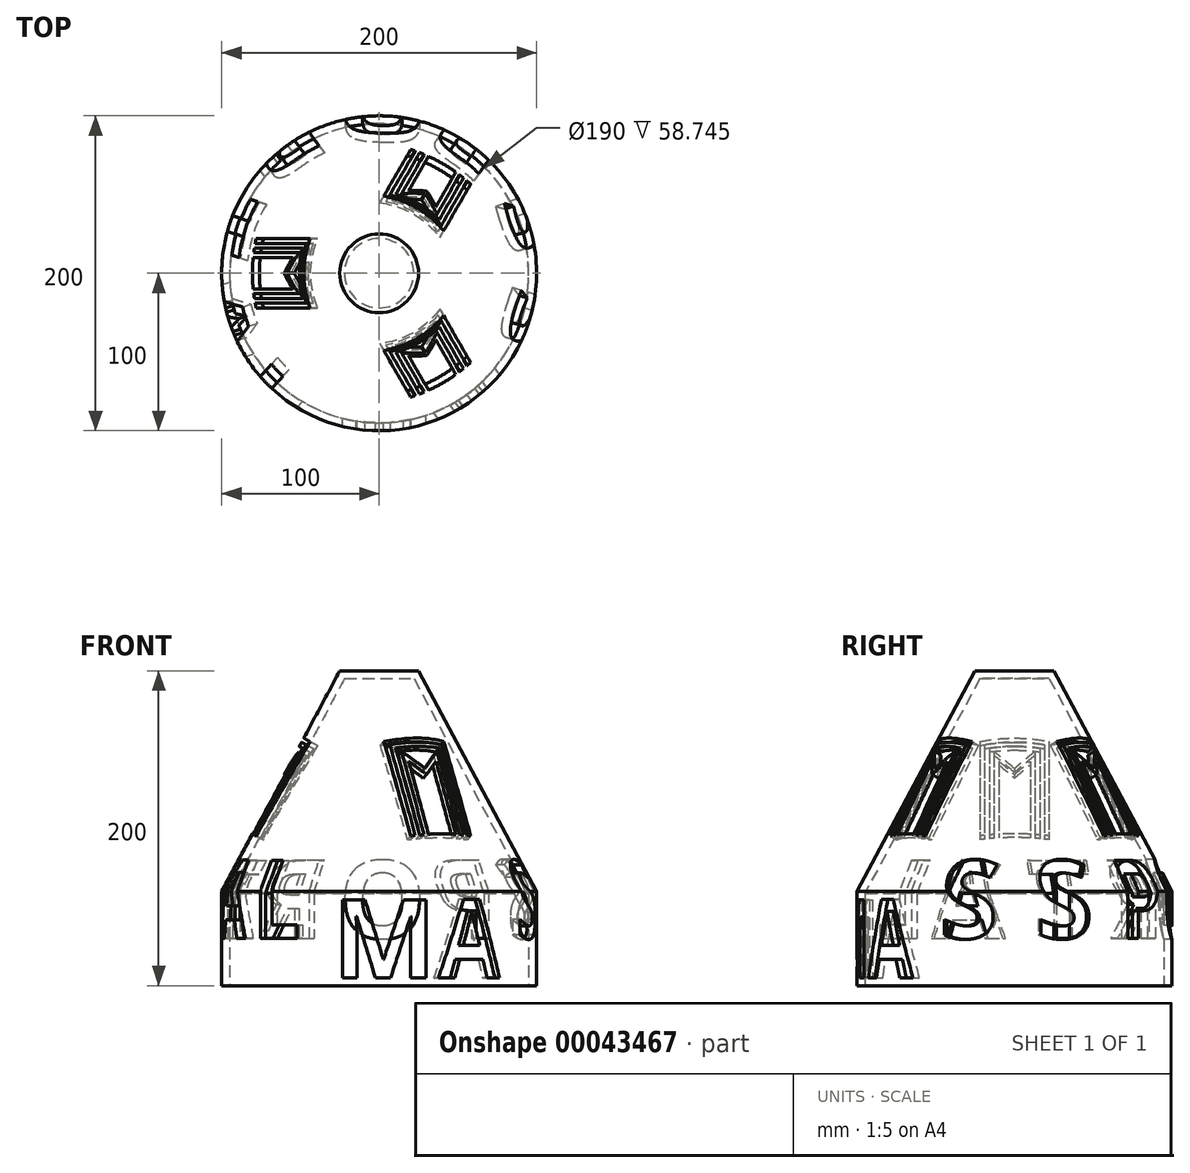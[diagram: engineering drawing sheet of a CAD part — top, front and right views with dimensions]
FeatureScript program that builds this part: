
annotation { "Feature Type Name" : "Feature", "Feature Type Description" : "" }
export const myFeature = defineFeature(function(context is Context, id is Id, definition is map)
    precondition{}
    {
        {
            var Q0;
            Q0=qCreatedBy(makeId("Front.planeOp"),FACE);
            var sketch = newSketch(context, id + "F0", { "sketchPlane" : qUnion([Q0])});
            skLineSegment(sketch, "E0", {"start": v(0, 0) * mm, "end": v(0, 200) * mm, "construction": true});
            skLineSegment(sketch, "E1", {"start": v(0, 200) * mm, "end": v(-25, 200) * mm});
            skLineSegment(sketch, "E2", {"start": v(-25, 200) * mm, "end": v(-100, 60) * mm});
            skLineSegment(sketch, "E3", {"start": v(-100, 60) * mm, "end": v(-100, 0) * mm});
            skLineSegment(sketch, "E4.0", {"start": v(-95, 58.75) * mm, "end": v(-95, 0) * mm});
            skLineSegment(sketch, "E4.1", {"start": v(-22, 195) * mm, "end": v(-95, 58.75) * mm});
            skLineSegment(sketch, "E4.2", {"start": v(0, 195) * mm, "end": v(-22, 195) * mm});
            skLineSegment(sketch, "E5", {"start": v(-100, 0) * mm, "end": v(-95, 0) * mm});
            skLineSegment(sketch, "E6", {"start": v(0, 200) * mm, "end": v(0, 195) * mm});
            skSolve(sketch);
        }
        {
            var Q0;
            Q0=makeQuery(id+"F0.imprint","IMPRINT",FACE,{"disambiguationData":[TD([[makeQuery(id+"F0.imprint","IMPRINT",EDGE,{"derivedFrom":sQuery(id+"F0.wireOp",EDGE,"E1")}),1.0]])]});
            var Q1;
            Q1=sQuery(id+"F0.wireOp",EDGE,"E0");
            revolve(context, id + "F1", {"entities" : qUnion([Q0]), "axis" : qUnion([Q1]), "revolveType" : RevolveType.FULL});
        }
        {
            var Q0;
            Q0=qCreatedBy(makeId("Front.planeOp"),FACE);
            var Q1;
            Q1=sQuery(id+"F0.wireOp",EDGE,"E0");
            cPlane(context, id + "F2", {"entities" : qUnion([Q0, Q1]), "cplaneType" : CPlaneType.LINE_ANGLE, "offset" : 150 * mm, "angle" : 36 * degree, "width" : 150 * mm, "height" : 150 * mm});
        }
        {
            var Q0;
            Q0=qCreatedBy(id+"F2.planeOp",FACE);
            var Q1;
            Q1=sQuery(id+"F0.wireOp",EDGE,"E0");
            cPlane(context, id + "F3", {"entities" : qUnion([Q0, Q1]), "cplaneType" : CPlaneType.LINE_ANGLE, "offset" : 150 * mm, "angle" : 36 * degree, "width" : 150 * mm, "height" : 150 * mm});
        }
        {
            var Q0;
            Q0=qCreatedBy(id+"F3.planeOp",FACE);
            var Q1;
            Q1=sQuery(id+"F0.wireOp",EDGE,"E0");
            cPlane(context, id + "F4", {"entities" : qUnion([Q0, Q1]), "cplaneType" : CPlaneType.LINE_ANGLE, "offset" : 150 * mm, "angle" : 36 * degree, "width" : 150 * mm, "height" : 150 * mm});
        }
        {
            var Q0;
            Q0=qCreatedBy(id+"F4.planeOp",FACE);
            var Q1;
            Q1=sQuery(id+"F0.wireOp",EDGE,"E0");
            cPlane(context, id + "F5", {"entities" : qUnion([Q0, Q1]), "cplaneType" : CPlaneType.LINE_ANGLE, "offset" : 150 * mm, "angle" : 36 * degree, "width" : 150 * mm, "height" : 150 * mm});
        }
        {
            var Q0;
            Q0=qCreatedBy(id+"F5.planeOp",FACE);
            var Q1;
            Q1=sQuery(id+"F0.wireOp",EDGE,"E0");
            cPlane(context, id + "F6", {"entities" : qUnion([Q0, Q1]), "cplaneType" : CPlaneType.LINE_ANGLE, "offset" : 150 * mm, "angle" : 36 * degree, "width" : 150 * mm, "height" : 150 * mm});
        }
        {
            var Q0;
            Q0=qCreatedBy(id+"F6.planeOp",FACE);
            var Q1;
            Q1=sQuery(id+"F0.wireOp",EDGE,"E0");
            cPlane(context, id + "F7", {"entities" : qUnion([Q0, Q1]), "cplaneType" : CPlaneType.LINE_ANGLE, "offset" : 150 * mm, "angle" : 36 * degree, "width" : 150 * mm, "height" : 150 * mm});
        }
        {
            var Q0;
            Q0=sQuery(id+"F0.wireOp",EDGE,"E0");
            var Q1;
            Q1=qCreatedBy(id+"F7.planeOp",FACE);
            cPlane(context, id + "F8", {"entities" : qUnion([Q0, Q1]), "cplaneType" : CPlaneType.LINE_ANGLE, "offset" : 150 * mm, "angle" : 36 * degree, "width" : 150 * mm, "height" : 150 * mm});
        }
        {
            var Q0;
            Q0=qCreatedBy(id+"F8.planeOp",FACE);
            var Q1;
            Q1=sQuery(id+"F0.wireOp",EDGE,"E0");
            cPlane(context, id + "F9", {"entities" : qUnion([Q0, Q1]), "cplaneType" : CPlaneType.LINE_ANGLE, "offset" : 150 * mm, "angle" : 36 * degree, "width" : 150 * mm, "height" : 150 * mm});
        }
        {
            var Q0;
            Q0=qCreatedBy(makeId("Front.planeOp"),FACE);
            var sketch = newSketch(context, id + "F10", { "sketchPlane" : qUnion([Q0])});
            skText(sketch, "E7", { "text": "M", "fontName": "OpenSans-Bold.ttf"});
            skLineSegment(sketch, "E8", {"start": v(0, 0) * mm, "end": v(0, 5) * mm, "construction": true});
            const initialGuessF10  = {"E7": [-0.02962, 0.005, 1, 0, 0.05]};
            skSetInitialGuess(sketch, initialGuessF10);
            skSolve(sketch);
        }
        {
            var Q0;
            Q0=qCreatedBy(id+"F2.planeOp",FACE);
            var sketch = newSketch(context, id + "F11", { "sketchPlane" : qUnion([Q0])});
            skText(sketch, "E9", { "text": "A", "fontName": "OpenSans-Bold.ttf"});
            const initialGuessF11  = {"E9": [-0.02396, 0.005, 1, 0, 0.05]};
            skSetInitialGuess(sketch, initialGuessF11);
            skSolve(sketch);
        }
        {
            var Q0;
            Q0=qCreatedBy(id+"F3.planeOp",FACE);
            var sketch = newSketch(context, id + "F12", { "sketchPlane" : qUnion([Q0])});
            skText(sketch, "E10", { "text": "S", "fontName": "OpenSans-Bold.ttf"});
            const initialGuessF12  = {"E10": [-0.01775, 0.03, 1, 0, 0.05]};
            skSetInitialGuess(sketch, initialGuessF12);
            skSolve(sketch);
        }
        {
            var Q0;
            Q0=qCreatedBy(id+"F3.planeOp",FACE);
            var sketch = newSketch(context, id + "F13", { "sketchPlane" : qUnion([Q0])});
            skLineSegment(sketch, "E11.0", {"start": v(0, 0) * mm, "end": v(0, 200) * mm, "construction": true});
            skSolve(sketch);
        }
        {
            var Q0;
            Q0=sQuery(id+"F13.wireOp",EDGE,"E11.0");
            cPlane(context, id + "F14", {"entities" : qUnion([Q0]), "cplaneType" : CPlaneType.LINE_ANGLE, "offset" : 150 * mm, "angle" : 18 * degree, "width" : 150 * mm, "height" : 150 * mm});
        }
        {
            var Q0;
            Q0=qCreatedBy(id+"F14.planeOp",FACE);
            var sketch = newSketch(context, id + "F15", { "sketchPlane" : qUnion([Q0])});
            skText(sketch, "E12", { "text": "S", "fontName": "OpenSans-Bold.ttf"});
            const initialGuessF15  = {"E12": [-0.01775, 0.03, 1, 0, 0.05]};
            skSetInitialGuess(sketch, initialGuessF15);
            skSolve(sketch);
        }
        {
            var Q0;
            Q0=qCreatedBy(id+"F5.planeOp",FACE);
            var sketch = newSketch(context, id + "F16", { "sketchPlane" : qUnion([Q0])});
            skText(sketch, "E13", { "text": "P", "fontName": "OpenSans-Bold.ttf"});
            const initialGuessF16  = {"E13": [-0.02024, 0.03, 1, 0, 0.05]};
            skSetInitialGuess(sketch, initialGuessF16);
            skSolve(sketch);
        }
        {
            var Q0;
            Q0=qCreatedBy(id+"F6.planeOp",FACE);
            var sketch = newSketch(context, id + "F17", { "sketchPlane" : qUnion([Q0])});
            skText(sketch, "E14", { "text": "O", "fontName": "OpenSans-Bold.ttf"});
            const initialGuessF17  = {"E14": [-0.02562, 0.03, 1, 0, 0.05]};
            skSetInitialGuess(sketch, initialGuessF17);
            skSolve(sketch);
        }
        {
            var Q0;
            Q0=qCreatedBy(id+"F7.planeOp",FACE);
            var sketch = newSketch(context, id + "F18", { "sketchPlane" : qUnion([Q0])});
            skText(sketch, "E15", { "text": "R", "fontName": "OpenSans-Bold.ttf"});
            const initialGuessF18  = {"E15": [-0.02292, 0.03, 1, 0, 0.05]};
            skSetInitialGuess(sketch, initialGuessF18);
            skSolve(sketch);
        }
        {
            var Q0;
            Q0=qCreatedBy(id+"F8.planeOp",FACE);
            var sketch = newSketch(context, id + "F19", { "sketchPlane" : qUnion([Q0])});
            skText(sketch, "E16", { "text": "T", "fontName": "OpenSans-Bold.ttf"});
            const initialGuessF19  = {"E16": [-0.01941, 0.03, 1, 0, 0.05]};
            skSetInitialGuess(sketch, initialGuessF19);
            skSolve(sketch);
        }
        {
            var Q0;
            Q0=qCreatedBy(id+"F9.planeOp",FACE);
            var sketch = newSketch(context, id + "F20", { "sketchPlane" : qUnion([Q0])});
            skText(sketch, "E17", { "text": "A", "fontName": "OpenSans-Bold.ttf"});
            const initialGuessF20  = {"E17": [-0.02396, 0.03, 1, 0, 0.05]};
            skSetInitialGuess(sketch, initialGuessF20);
            skSolve(sketch);
        }
        {
            var Q0;
            Q0=qCreatedBy(id+"F9.planeOp",FACE);
            var sketch = newSketch(context, id + "F21", { "sketchPlane" : qUnion([Q0])});
            skLineSegment(sketch, "E18.0", {"start": v(0, 0) * mm, "end": v(0, 200) * mm, "construction": true});
            skSolve(sketch);
        }
        {
            var Q0;
            Q0=sQuery(id+"F21.wireOp",EDGE,"E18.0");
            cPlane(context, id + "F22", {"entities" : qUnion([Q0]), "cplaneType" : CPlaneType.LINE_ANGLE, "offset" : 150 * mm, "angle" : 228 * degree, "width" : 150 * mm, "height" : 150 * mm});
        }
        {
            var Q0;
            Q0=qCreatedBy(id+"F22.planeOp",FACE);
            var sketch = newSketch(context, id + "F23", { "sketchPlane" : qUnion([Q0])});
            skText(sketch, "E19", { "text": "L", "fontName": "OpenSans-Bold.ttf"});
            const initialGuessF23  = {"E19": [-0.01843, 0.03, 1, 0, 0.05]};
            skSetInitialGuess(sketch, initialGuessF23);
            skSolve(sketch);
        }
        {
            var Q0;
            Q0 = qSketchRegion(id + "F10", true);
            extrude(context, id + "F24", {"entities" : qUnion([Q0]), "operationType" : NewBodyOperationType.REMOVE, "endBound" : BoundingType.THROUGH_ALL, "depth" : 25 * mm});
        }
        {
            var Q0;
            Q0 = qSketchRegion(id + "F11", true);
            extrude(context, id + "F25", {"entities" : qUnion([Q0]), "operationType" : NewBodyOperationType.REMOVE, "endBound" : BoundingType.THROUGH_ALL, "oppositeDirection" : true, "depth" : 25 * mm});
        }
        {
            var Q0;
            Q0 = qSketchRegion(id + "F12", true);
            extrude(context, id + "F26", {"entities" : qUnion([Q0]), "operationType" : NewBodyOperationType.REMOVE, "endBound" : BoundingType.THROUGH_ALL, "depth" : 25 * mm});
        }
        {
            var Q0;
            Q0 = qSketchRegion(id + "F15", true);
            extrude(context, id + "F27", {"entities" : qUnion([Q0]), "operationType" : NewBodyOperationType.REMOVE, "endBound" : BoundingType.THROUGH_ALL, "depth" : 25 * mm});
        }
        {
            var Q0;
            Q0 = qSketchRegion(id + "F16", true);
            extrude(context, id + "F28", {"entities" : qUnion([Q0]), "operationType" : NewBodyOperationType.REMOVE, "endBound" : BoundingType.THROUGH_ALL, "depth" : 25 * mm});
        }
        {
            var Q0;
            Q0 = qSketchRegion(id + "F17", true);
            extrude(context, id + "F29", {"entities" : qUnion([Q0]), "operationType" : NewBodyOperationType.REMOVE, "endBound" : BoundingType.THROUGH_ALL, "oppositeDirection" : true, "depth" : 25 * mm});
        }
        {
            var Q0;
            Q0 = qSketchRegion(id + "F18", true);
            extrude(context, id + "F30", {"entities" : qUnion([Q0]), "operationType" : NewBodyOperationType.REMOVE, "endBound" : BoundingType.THROUGH_ALL, "depth" : 25 * mm});
        }
        {
            var Q0;
            Q0 = qSketchRegion(id + "F19", true);
            extrude(context, id + "F31", {"entities" : qUnion([Q0]), "operationType" : NewBodyOperationType.REMOVE, "endBound" : BoundingType.THROUGH_ALL, "oppositeDirection" : true, "depth" : 25 * mm});
        }
        {
            var Q0;
            Q0 = qSketchRegion(id + "F20", true);
            extrude(context, id + "F32", {"entities" : qUnion([Q0]), "operationType" : NewBodyOperationType.REMOVE, "endBound" : BoundingType.THROUGH_ALL, "depth" : 25 * mm});
        }
        {
            var Q0;
            Q0 = qSketchRegion(id + "F23", true);
            extrude(context, id + "F33", {"entities" : qUnion([Q0]), "operationType" : NewBodyOperationType.REMOVE, "endBound" : BoundingType.THROUGH_ALL, "depth" : 25 * mm});
        }
        {
            var Q0;
            Q0=sQuery(id+"F0.wireOp",EDGE,"E4.1");
            cPlane(context, id + "F34", {"entities" : qUnion([Q0]), "cplaneType" : CPlaneType.LINE_ANGLE, "offset" : 150 * mm, "angle" : 0 * degree, "width" : 150 * mm, "height" : 150 * mm});
        }
        {
            var Q0;
            Q0=qCreatedBy(id+"F34.planeOp",FACE);
            var sketch = newSketch(context, id + "F35", { "sketchPlane" : qUnion([Q0])});
            skLineSegment(sketch, "E20.rect.bottom", {"start": v(25, 119) * mm, "end": v(-25, 119) * mm});
            skLineSegment(sketch, "E20.rect.top", {"start": v(25, 44) * mm, "end": v(10, 44) * mm});
            skLineSegment(sketch, "E20.rect.left", {"start": v(25, 119) * mm, "end": v(25, 44) * mm});
            skLineSegment(sketch, "E20.rect.right", {"start": v(-25, 119) * mm, "end": v(-25, 44) * mm});
            skPoint(sketch, "E20.rect.middle", {"position": v(0, 81.5) * mm});
            skLineSegment(sketch, "E21.0", {"start": v(-22, 116) * mm, "end": v(-22, 47) * mm});
            skLineSegment(sketch, "E21.1", {"start": v(22, 116) * mm, "end": v(-22, 116) * mm});
            skLineSegment(sketch, "E21.2", {"start": v(22, 116) * mm, "end": v(22, 47) * mm});
            skLineSegment(sketch, "E22.0", {"start": v(-19, 113) * mm, "end": v(-19, 47) * mm});
            skLineSegment(sketch, "E22.1", {"start": v(19, 113) * mm, "end": v(-19, 113) * mm});
            skLineSegment(sketch, "E22.2", {"start": v(19, 113) * mm, "end": v(19, 47) * mm});
            skLineSegment(sketch, "E23.0", {"start": v(-16, 110) * mm, "end": v(-16, 47) * mm});
            skLineSegment(sketch, "E23.1", {"start": v(16, 110) * mm, "end": v(-16, 110) * mm});
            skLineSegment(sketch, "E23.2", {"start": v(16, 110) * mm, "end": v(16, 47) * mm});
            skLineSegment(sketch, "E24.0", {"start": v(-13, 107) * mm, "end": v(-13, 47) * mm});
            skLineSegment(sketch, "E24.2", {"start": v(13, 107) * mm, "end": v(13, 47) * mm});
            skLineSegment(sketch, "E25.0", {"start": v(-10, 99.75) * mm, "end": v(-10, 44) * mm});
            skLineSegment(sketch, "E25.2", {"start": v(10, 99.75) * mm, "end": v(10, 44) * mm});
            skLineSegment(sketch, "E26", {"start": v(-22, 47) * mm, "end": v(-19, 47) * mm});
            skLineSegment(sketch, "E27", {"start": v(-16, 47) * mm, "end": v(-13, 47) * mm});
            skLineSegment(sketch, "E28", {"start": v(13, 47) * mm, "end": v(16, 47) * mm});
            skLineSegment(sketch, "E29", {"start": v(19, 47) * mm, "end": v(22, 47) * mm});
            skLineSegment(sketch, "E30.trimOffspring", {"start": v(-10, 44) * mm, "end": v(-25, 44) * mm});
            skLineSegment(sketch, "E31", {"start": v(-13, 107) * mm, "end": v(0, 94) * mm});
            skLineSegment(sketch, "E32", {"start": v(0, 94) * mm, "end": v(13, 107) * mm});
            skLineSegment(sketch, "E33", {"start": v(10, 99.75) * mm, "end": v(0, 89.75) * mm});
            skLineSegment(sketch, "E34", {"start": v(0, 89.75) * mm, "end": v(-10, 99.75) * mm});
            skLineSegment(sketch, "E35", {"start": v(-10, 47) * mm, "end": v(10, 47) * mm});
            skSolve(sketch);
        }
        {
            var Q0;
            Q0=makeQuery(id+"F35.imprint","IMPRINT",FACE,{"disambiguationData":[TD([[makeQuery(id+"F35.imprint","IMPRINT",EDGE,{"derivedFrom":sQuery(id+"F35.wireOp",EDGE,"E25.0")}),1.0]])]});
            var Q1;
            Q1=makeQuery(id+"F35.imprint","IMPRINT",FACE,{"disambiguationData":[TD([[makeQuery(id+"F35.imprint","IMPRINT",EDGE,{"derivedFrom":sQuery(id+"F35.wireOp",EDGE,"E23.0")}),1.0]])]});
            var Q2;
            Q2=makeQuery(id+"F35.imprint","IMPRINT",FACE,{"disambiguationData":[TD([[makeQuery(id+"F35.imprint","IMPRINT",EDGE,{"derivedFrom":sQuery(id+"F35.wireOp",EDGE,"E21.0")}),1.0]])]});
            extrude(context, id + "F36", {"entities" : qUnion([Q0, Q1, Q2]), "depth" : 10 * mm, "hasSecondDirection" : true, "secondDirectionOppositeDirection" : true, "secondDirectionDepth" : 10 * mm});
        }
        {
            var Q0;
            Q0=makeQuery(id+"F36.opExtrude","SWEPT_BODY",BODY,{"disambiguationData":[OSD([sQuery(id+"F35.wireOp",EDGE,"E21.0"),sQuery(id+"F35.wireOp",EDGE,"E21.1"),sQuery(id+"F35.wireOp",EDGE,"E21.2"),sQuery(id+"F35.wireOp",EDGE,"E22.0"),sQuery(id+"F35.wireOp",EDGE,"E22.1"),sQuery(id+"F35.wireOp",EDGE,"E22.2"),sQuery(id+"F35.wireOp",EDGE,"E26"),sQuery(id+"F35.wireOp",EDGE,"E29")])]});
            var Q1;
            Q1=makeQuery(id+"F36.opExtrude","SWEPT_BODY",BODY,{"disambiguationData":[OSD([sQuery(id+"F35.wireOp",EDGE,"E23.0"),sQuery(id+"F35.wireOp",EDGE,"E23.1"),sQuery(id+"F35.wireOp",EDGE,"E23.2"),sQuery(id+"F35.wireOp",EDGE,"E24.0"),sQuery(id+"F35.wireOp",EDGE,"E24.2"),sQuery(id+"F35.wireOp",EDGE,"E27"),sQuery(id+"F35.wireOp",EDGE,"E28"),sQuery(id+"F35.wireOp",EDGE,"E31"),sQuery(id+"F35.wireOp",EDGE,"E32")])]});
            var Q2;
            Q2=makeQuery(id+"F36.opExtrude","SWEPT_BODY",BODY,{"disambiguationData":[OSD([sQuery(id+"F35.wireOp",EDGE,"E25.0"),sQuery(id+"F35.wireOp",EDGE,"E25.2"),sQuery(id+"F35.wireOp",EDGE,"E33"),sQuery(id+"F35.wireOp",EDGE,"E34"),sQuery(id+"F35.wireOp",EDGE,"E35")])]});
            var Q3;
            Q3=makeQuery(id+"F1.opRevolve","SWEPT_EDGE",EDGE,{"disambiguationData":[OSD([sQuery(id+"F0.wireOp",EDGE,"E1"),sQuery(id+"F0.wireOp",EDGE,"E2")])]});
            circularPattern(context, id + "F37", {"entities" : qUnion([Q0, Q1, Q2]), "axis" : qUnion([Q3]), "angle" : 360 * degree, "instanceCount" : 3, "equalSpace" : true});
        }
        {
            var Q0;
            Q0=makeQuery(id+"F37.opPattern","COPY",BODY,{"derivedFrom":makeQuery(id+"F36.opExtrude","SWEPT_BODY",BODY,{"disambiguationData":[OSD([sQuery(id+"F35.wireOp",EDGE,"E25.0"),sQuery(id+"F35.wireOp",EDGE,"E25.2"),sQuery(id+"F35.wireOp",EDGE,"E33"),sQuery(id+"F35.wireOp",EDGE,"E34"),sQuery(id+"F35.wireOp",EDGE,"E35")])]}),"instanceName":"1"});
            var Q1;
            Q1=makeQuery(id+"F37.opPattern","COPY",BODY,{"derivedFrom":makeQuery(id+"F36.opExtrude","SWEPT_BODY",BODY,{"disambiguationData":[OSD([sQuery(id+"F35.wireOp",EDGE,"E23.0"),sQuery(id+"F35.wireOp",EDGE,"E23.1"),sQuery(id+"F35.wireOp",EDGE,"E23.2"),sQuery(id+"F35.wireOp",EDGE,"E24.0"),sQuery(id+"F35.wireOp",EDGE,"E24.2"),sQuery(id+"F35.wireOp",EDGE,"E27"),sQuery(id+"F35.wireOp",EDGE,"E28"),sQuery(id+"F35.wireOp",EDGE,"E31"),sQuery(id+"F35.wireOp",EDGE,"E32")])]}),"instanceName":"1"});
            var Q2;
            Q2=makeQuery(id+"F37.opPattern","COPY",BODY,{"derivedFrom":makeQuery(id+"F36.opExtrude","SWEPT_BODY",BODY,{"disambiguationData":[OSD([sQuery(id+"F35.wireOp",EDGE,"E21.0"),sQuery(id+"F35.wireOp",EDGE,"E21.1"),sQuery(id+"F35.wireOp",EDGE,"E21.2"),sQuery(id+"F35.wireOp",EDGE,"E22.0"),sQuery(id+"F35.wireOp",EDGE,"E22.1"),sQuery(id+"F35.wireOp",EDGE,"E22.2"),sQuery(id+"F35.wireOp",EDGE,"E26"),sQuery(id+"F35.wireOp",EDGE,"E29")])]}),"instanceName":"1"});
            var Q3;
            Q3=makeQuery(id+"F36.opExtrude","SWEPT_BODY",BODY,{"disambiguationData":[OSD([sQuery(id+"F35.wireOp",EDGE,"E21.0"),sQuery(id+"F35.wireOp",EDGE,"E21.1"),sQuery(id+"F35.wireOp",EDGE,"E21.2"),sQuery(id+"F35.wireOp",EDGE,"E22.0"),sQuery(id+"F35.wireOp",EDGE,"E22.1"),sQuery(id+"F35.wireOp",EDGE,"E22.2"),sQuery(id+"F35.wireOp",EDGE,"E26"),sQuery(id+"F35.wireOp",EDGE,"E29")])]});
            var Q4;
            Q4=makeQuery(id+"F36.opExtrude","SWEPT_BODY",BODY,{"disambiguationData":[OSD([sQuery(id+"F35.wireOp",EDGE,"E23.0"),sQuery(id+"F35.wireOp",EDGE,"E23.1"),sQuery(id+"F35.wireOp",EDGE,"E23.2"),sQuery(id+"F35.wireOp",EDGE,"E24.0"),sQuery(id+"F35.wireOp",EDGE,"E24.2"),sQuery(id+"F35.wireOp",EDGE,"E27"),sQuery(id+"F35.wireOp",EDGE,"E28"),sQuery(id+"F35.wireOp",EDGE,"E31"),sQuery(id+"F35.wireOp",EDGE,"E32")])]});
            var Q5;
            Q5=makeQuery(id+"F36.opExtrude","SWEPT_BODY",BODY,{"disambiguationData":[OSD([sQuery(id+"F35.wireOp",EDGE,"E25.0"),sQuery(id+"F35.wireOp",EDGE,"E25.2"),sQuery(id+"F35.wireOp",EDGE,"E33"),sQuery(id+"F35.wireOp",EDGE,"E34"),sQuery(id+"F35.wireOp",EDGE,"E35")])]});
            var Q6;
            Q6=makeQuery(id+"F37.opPattern","COPY",BODY,{"derivedFrom":makeQuery(id+"F36.opExtrude","SWEPT_BODY",BODY,{"disambiguationData":[OSD([sQuery(id+"F35.wireOp",EDGE,"E25.0"),sQuery(id+"F35.wireOp",EDGE,"E25.2"),sQuery(id+"F35.wireOp",EDGE,"E33"),sQuery(id+"F35.wireOp",EDGE,"E34"),sQuery(id+"F35.wireOp",EDGE,"E35")])]}),"instanceName":"2"});
            var Q7;
            Q7=makeQuery(id+"F37.opPattern","COPY",BODY,{"derivedFrom":makeQuery(id+"F36.opExtrude","SWEPT_BODY",BODY,{"disambiguationData":[OSD([sQuery(id+"F35.wireOp",EDGE,"E23.0"),sQuery(id+"F35.wireOp",EDGE,"E23.1"),sQuery(id+"F35.wireOp",EDGE,"E23.2"),sQuery(id+"F35.wireOp",EDGE,"E24.0"),sQuery(id+"F35.wireOp",EDGE,"E24.2"),sQuery(id+"F35.wireOp",EDGE,"E27"),sQuery(id+"F35.wireOp",EDGE,"E28"),sQuery(id+"F35.wireOp",EDGE,"E31"),sQuery(id+"F35.wireOp",EDGE,"E32")])]}),"instanceName":"2"});
            var Q8;
            Q8=makeQuery(id+"F37.opPattern","COPY",BODY,{"derivedFrom":makeQuery(id+"F36.opExtrude","SWEPT_BODY",BODY,{"disambiguationData":[OSD([sQuery(id+"F35.wireOp",EDGE,"E21.0"),sQuery(id+"F35.wireOp",EDGE,"E21.1"),sQuery(id+"F35.wireOp",EDGE,"E21.2"),sQuery(id+"F35.wireOp",EDGE,"E22.0"),sQuery(id+"F35.wireOp",EDGE,"E22.1"),sQuery(id+"F35.wireOp",EDGE,"E22.2"),sQuery(id+"F35.wireOp",EDGE,"E26"),sQuery(id+"F35.wireOp",EDGE,"E29")])]}),"instanceName":"2"});
            var Q9;
            Q9=makeQuery(id+"F32.boolean.opBoolean","SPLIT",BODY,{"disambiguationData":[OD(0.0)],"derivedFrom":makeQuery(id+"F30.boolean.opBoolean","SPLIT",BODY,{"disambiguationData":[OD(0.0)],"derivedFrom":makeQuery(id+"F29.boolean.opBoolean","SPLIT",BODY,{"disambiguationData":[OD(0.0)],"derivedFrom":makeQuery(id+"F28.boolean.opBoolean","SPLIT",BODY,{"disambiguationData":[OD(0.0)],"derivedFrom":makeQuery(id+"F25.boolean.opBoolean","SPLIT",BODY,{"disambiguationData":[OD(0.0)],"derivedFrom":makeQuery(id+"F1.opRevolve","SWEPT_BODY",BODY,{"disambiguationData":[OSD([sQuery(id+"F0.wireOp",EDGE,"E1"),sQuery(id+"F0.wireOp",EDGE,"E2"),sQuery(id+"F0.wireOp",EDGE,"E3"),sQuery(id+"F0.wireOp",EDGE,"E4.0"),sQuery(id+"F0.wireOp",EDGE,"E4.1"),sQuery(id+"F0.wireOp",EDGE,"E4.2"),sQuery(id+"F0.wireOp",EDGE,"E5"),sQuery(id+"F0.wireOp",EDGE,"E6")])]})})})})})});
            booleanBodies(context, id + "F38", {"operationType" : BooleanOperationType.SUBTRACTION, "tools" : qUnion([Q0, Q1, Q2, Q3, Q4, Q5, Q6, Q7, Q8]), "targets" : qUnion([Q9])});
        }
    });
